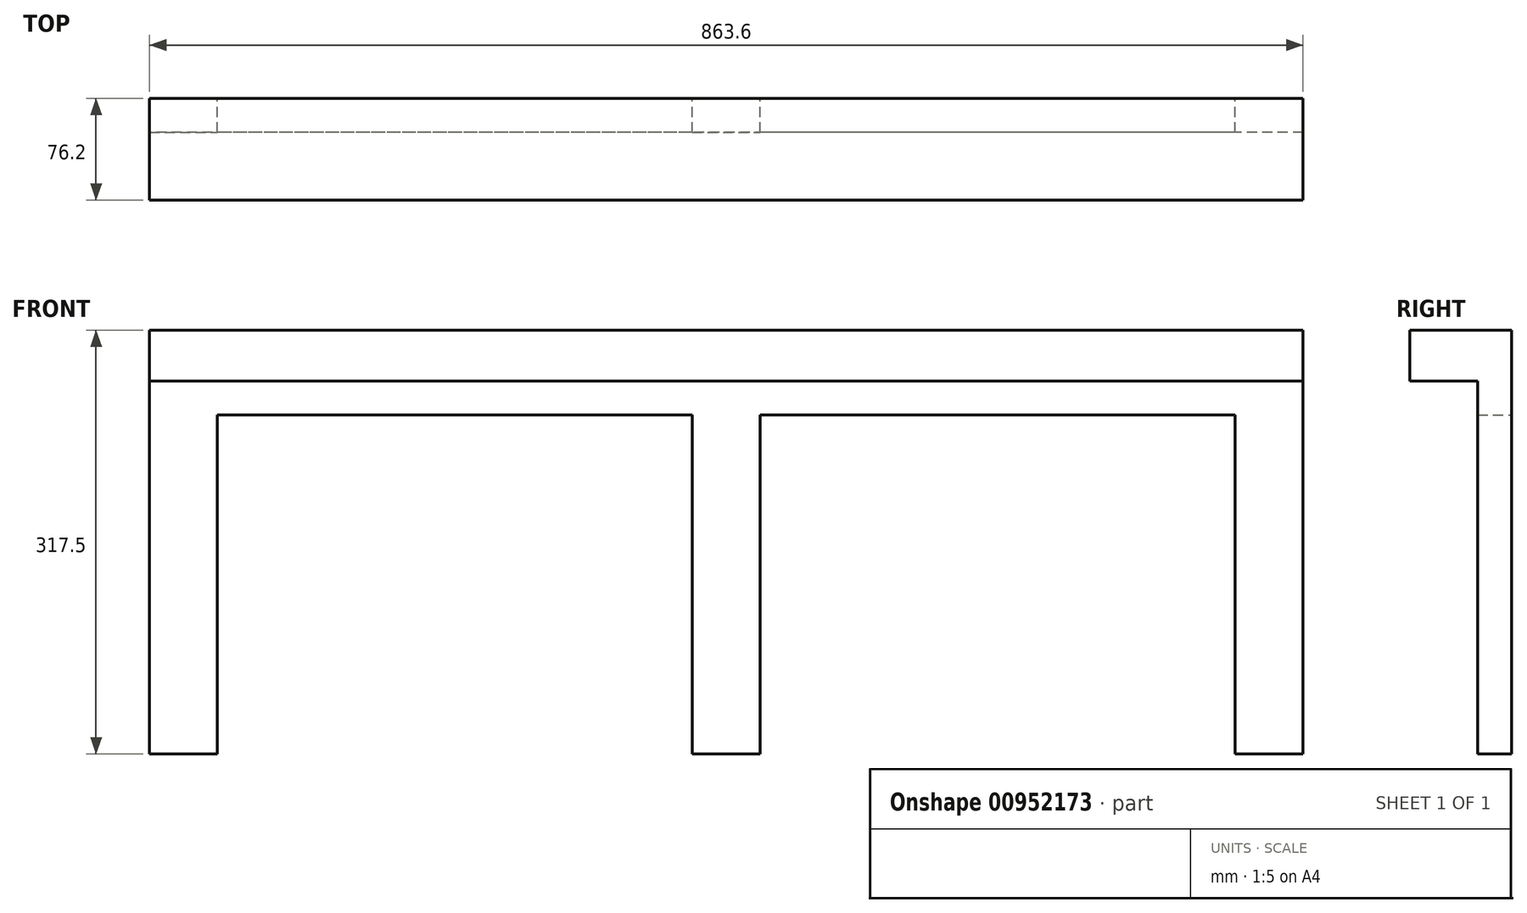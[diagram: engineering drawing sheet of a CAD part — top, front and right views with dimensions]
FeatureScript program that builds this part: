
annotation { "Feature Type Name" : "Feature", "Feature Type Description" : "" }
export const myFeature = defineFeature(function(context is Context, id is Id, definition is map)
    precondition{}
    {
        {
            var Q0;
            Q0=qCreatedBy(makeId("Front.planeOp"),FACE);
            var sketch = newSketch(context, id + "F0", { "sketchPlane" : qUnion([Q0])});
            skLineSegment(sketch, "E0.bottom", {"start": v(431.8, 37) * mm, "end": v(-431.8, 37) * mm});
            skLineSegment(sketch, "E0.top", {"start": v(431.8, 87.8) * mm, "end": v(-431.8, 87.8) * mm});
            skLineSegment(sketch, "E0.left", {"start": v(431.8, 37) * mm, "end": v(431.8, 87.8) * mm});
            skLineSegment(sketch, "E0.right", {"start": v(-431.8, 37) * mm, "end": v(-431.8, 87.8) * mm});
            skPoint(sketch, "E0.middle", {"position": v(0, 62.4) * mm});
            skLineSegment(sketch, "E1.bottom", {"start": v(431.8, 87.8) * mm, "end": v(381, 87.8) * mm});
            skLineSegment(sketch, "E1.top", {"start": v(431.8, -217) * mm, "end": v(381, -217) * mm});
            skLineSegment(sketch, "E1.left", {"start": v(431.8, 87.8) * mm, "end": v(431.8, -217) * mm});
            skLineSegment(sketch, "E1.right", {"start": v(381, 87.8) * mm, "end": v(381, -217) * mm});
            skLineSegment(sketch, "E2.MirrorCS", {"start": v(-431.8, -217) * mm, "end": v(-381, -217) * mm});
            skLineSegment(sketch, "E3.MirrorCS", {"start": v(-381, 87.8) * mm, "end": v(-381, -217) * mm});
            skLineSegment(sketch, "E4.MirrorCS", {"start": v(-431.8, 87.8) * mm, "end": v(-431.8, -217) * mm});
            skLineSegment(sketch, "E5.bottom", {"start": v(-25.4, 37) * mm, "end": v(25.4, 37) * mm});
            skLineSegment(sketch, "E5.top", {"start": v(-25.4, -217) * mm, "end": v(25.4, -217) * mm});
            skLineSegment(sketch, "E5.left", {"start": v(-25.4, 37) * mm, "end": v(-25.4, -217) * mm});
            skLineSegment(sketch, "E5.right", {"start": v(25.4, 37) * mm, "end": v(25.4, -217) * mm});
            skSolve(sketch);
        }
        {
            var Q0;
            Q0 = qSketchRegion(id + "F0", true);
            extrude(context, id + "F1", {"entities" : qUnion([Q0]), "depth" : 25.4 * mm, "offsetDistance" : 25.4 * mm});
        }
        {
            var Q0;
            Q0=makeQuery(id+"F1.opExtrude","CAP_FACE",FACE,{"disambiguationData":[OSD([sQuery(id+"F0.wireOp",EDGE,"E0.bottom"),sQuery(id+"F0.wireOp",EDGE,"E0.top"),sQuery(id+"F0.wireOp",EDGE,"E1.bottom"),sQuery(id+"F0.wireOp",EDGE,"E1.top"),sQuery(id+"F0.wireOp",EDGE,"E1.left"),sQuery(id+"F0.wireOp",EDGE,"E1.right"),sQuery(id+"F0.wireOp",EDGE,"E2.MirrorCS"),sQuery(id+"F0.wireOp",EDGE,"E3.MirrorCS"),sQuery(id+"F0.wireOp",EDGE,"E4.MirrorCS")])],"isStart":false});
            var sketch = newSketch(context, id + "F2", { "sketchPlane" : qUnion([Q0])});
            skLineSegment(sketch, "E6.bottom", {"start": v(-431.8, 87.8) * mm, "end": v(431.8, 87.8) * mm});
            skLineSegment(sketch, "E6.top", {"start": v(-431.8, 62.4) * mm, "end": v(431.8, 62.4) * mm});
            skLineSegment(sketch, "E6.left", {"start": v(-431.8, 87.8) * mm, "end": v(-431.8, 62.4) * mm});
            skLineSegment(sketch, "E6.right", {"start": v(431.8, 87.8) * mm, "end": v(431.8, 62.4) * mm});
            skLineSegment(sketch, "E7.bottom", {"start": v(431.8, 87.8) * mm, "end": v(-431.8, 87.8) * mm});
            skLineSegment(sketch, "E7.top", {"start": v(431.8, 100.5) * mm, "end": v(-431.8, 100.5) * mm});
            skLineSegment(sketch, "E7.left", {"start": v(431.8, 87.8) * mm, "end": v(431.8, 100.5) * mm});
            skLineSegment(sketch, "E7.right", {"start": v(-431.8, 87.8) * mm, "end": v(-431.8, 100.5) * mm});
            skSolve(sketch);
        }
        {
            var Q0;
            Q0 = qSketchRegion(id + "F2", true);
            extrude(context, id + "F3", {"entities" : qUnion([Q0]), "operationType" : NewBodyOperationType.ADD, "depth" : 50.8 * mm, "offsetDistance" : 25.4 * mm, "hasSecondDirection" : true, "secondDirectionOppositeDirection" : true, "secondDirectionDepth" : 25.4 * mm});
        }
    });
